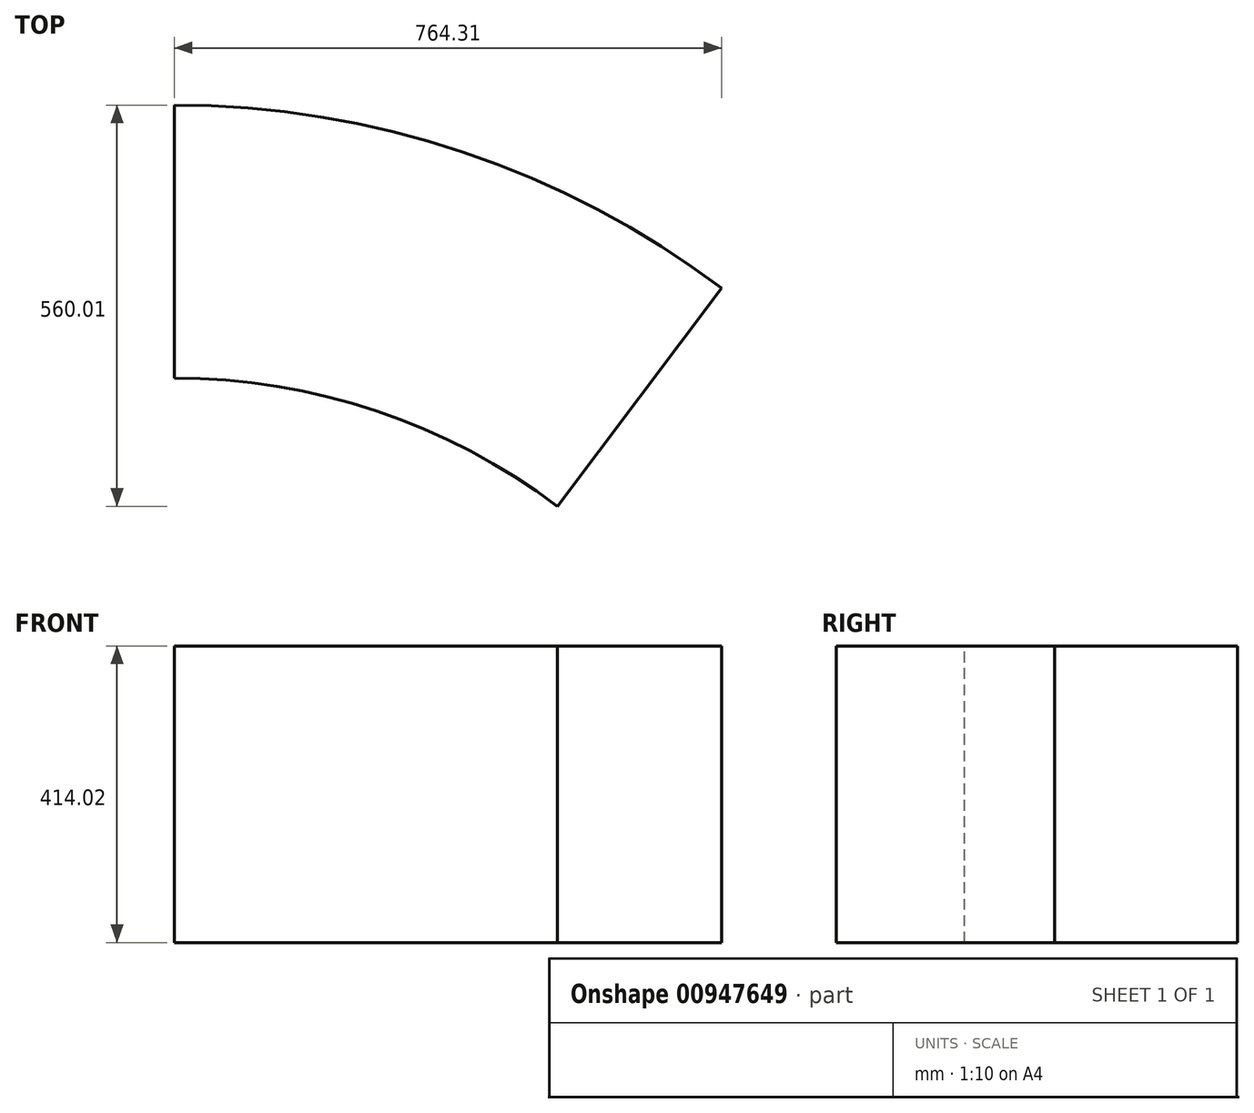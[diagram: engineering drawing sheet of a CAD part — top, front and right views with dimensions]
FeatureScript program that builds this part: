
annotation { "Feature Type Name" : "Feature", "Feature Type Description" : "" }
export const myFeature = defineFeature(function(context is Context, id is Id, definition is map)
    precondition{}
    {
        {
            var Q0;
            Q0=qCreatedBy(makeId("Top.planeOp"),FACE);
            var sketch = newSketch(context, id + "F0", { "sketchPlane" : qUnion([Q0])});
            skCircle(sketch, "E0", {"center": v(0, 0) * mm, "radius": 1270 * mm});
            skCircle(sketch, "E1", {"center": v(0, 0) * mm, "radius": 889 * mm});
            skSolve(sketch);
        }
        {
            var Q0;
            Q0=qCreatedBy(makeId("Top.planeOp"),FACE);
            var sketch = newSketch(context, id + "F1", { "sketchPlane" : qUnion([Q0])});
            skLineSegment(sketch, "E2", {"start": v(0, 889) * mm, "end": v(0, 1270) * mm});
            skArc(sketch, "E3.0", {"start": v(764.3, 1014.27) * mm, "mid": v(402.98, 1204.37) * mm, "end": v(0, 1270) * mm});
            skArc(sketch, "E4.0", {"start": v(535.01, 709.99) * mm, "mid": v(282.08, 843.06) * mm, "end": v(0, 889) * mm});
            skLineSegment(sketch, "E5", {"start": v(535.01, 709.99) * mm, "end": v(764.3, 1014.27) * mm});
            skSolve(sketch);
        }
        {
            var Q0;
            Q0 = qSketchRegion(id + "F1", true);
            extrude(context, id + "F2", {"entities" : qUnion([Q0]), "oppositeDirection" : true, "depth" : 414.02 * mm, "offsetDistance" : 25.4 * mm});
        }
    });
